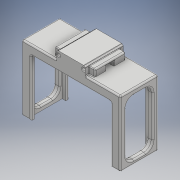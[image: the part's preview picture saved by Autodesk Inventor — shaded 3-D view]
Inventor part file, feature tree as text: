
AUTODESK INVENTOR PART (.ipt)
format: ipt  version: 2018 (Build 220112000, 112)  size: 1,244,672 bytes
history: native  units: mm
features: fillet x6, extrude x5, sketch x5, projected_geometry x3, mirror x2, chamfer x1, plane x1
ambient origin geometry x8: Origin, YZ Plane, XZ Plane, XY Plane, X Axis, Y Axis, Z Axis, Center Point
bodies: Solid1 (feature_tree)
feature tree (23):
  extrude  "Extrusion1"  Depth=0.25mm
  extrude  "Extrusion2"  Depth=0.5mm
  mirror  "Mirror1"
  chamfer  "Chamfer1"  Distance=4.0mm
  fillet  "Fillet1"  Radius=26.0mm
  extrude  "Extrusion3"  Depth=2.5mm
  extrude  "Extrusion4"  Depth=2.5mm
  fillet  "Fillet3"  Radius=2.5mm
  fillet  "Fillet4"  Radius=2.25mm
  extrude  "Extrusion5"  Depth=1.0mm TaperAngle=45.0deg
  plane  "Work Plane1"
  mirror  "Mirror2"
  fillet  "Fillet5"  Radius=0.4mm
  fillet  "Fillet6"  Radius=1.0mm
  fillet  "Fillet7"  Radius=5.2mm
  sketch  "Sketch1"  dims[d0=0.25mm d1=0.25mm]
  sketch  "Sketch2"  dims[d2=0.25mm d3=0.5mm]
  projected_geometry  "Projected Loop1"
  sketch  "Sketch3"  dims[d4=59.5mm]
  sketch  "Sketch4"  dims[d5=41.0mm]
  projected_geometry  "Projected Loop2"
  sketch  "Sketch5"  dims[d6=4.0mm d7=4.0mm d8=26.0mm d9=0.0mm d10=2.5mm d11=2.5mm d12=2.5mm d13=2.25mm d14=0.0mm d15=1.0mm d16=2.0mm d17=45.0deg d18=0.4mm d19=1.0mm d20=5.2mm d21=3.0mm d22=2.5mm d23=0.0mm d25=3.0mm d26=2.5mm d27=0.0mm d28=5.0mm d29=1.0mm d30=2.5mm d31=2.5mm d32=4.0mm d33=0.0mm d34=0.5mm d35=0.5mm d36=1.0mm]
  projected_geometry  "Projected Loop3"
